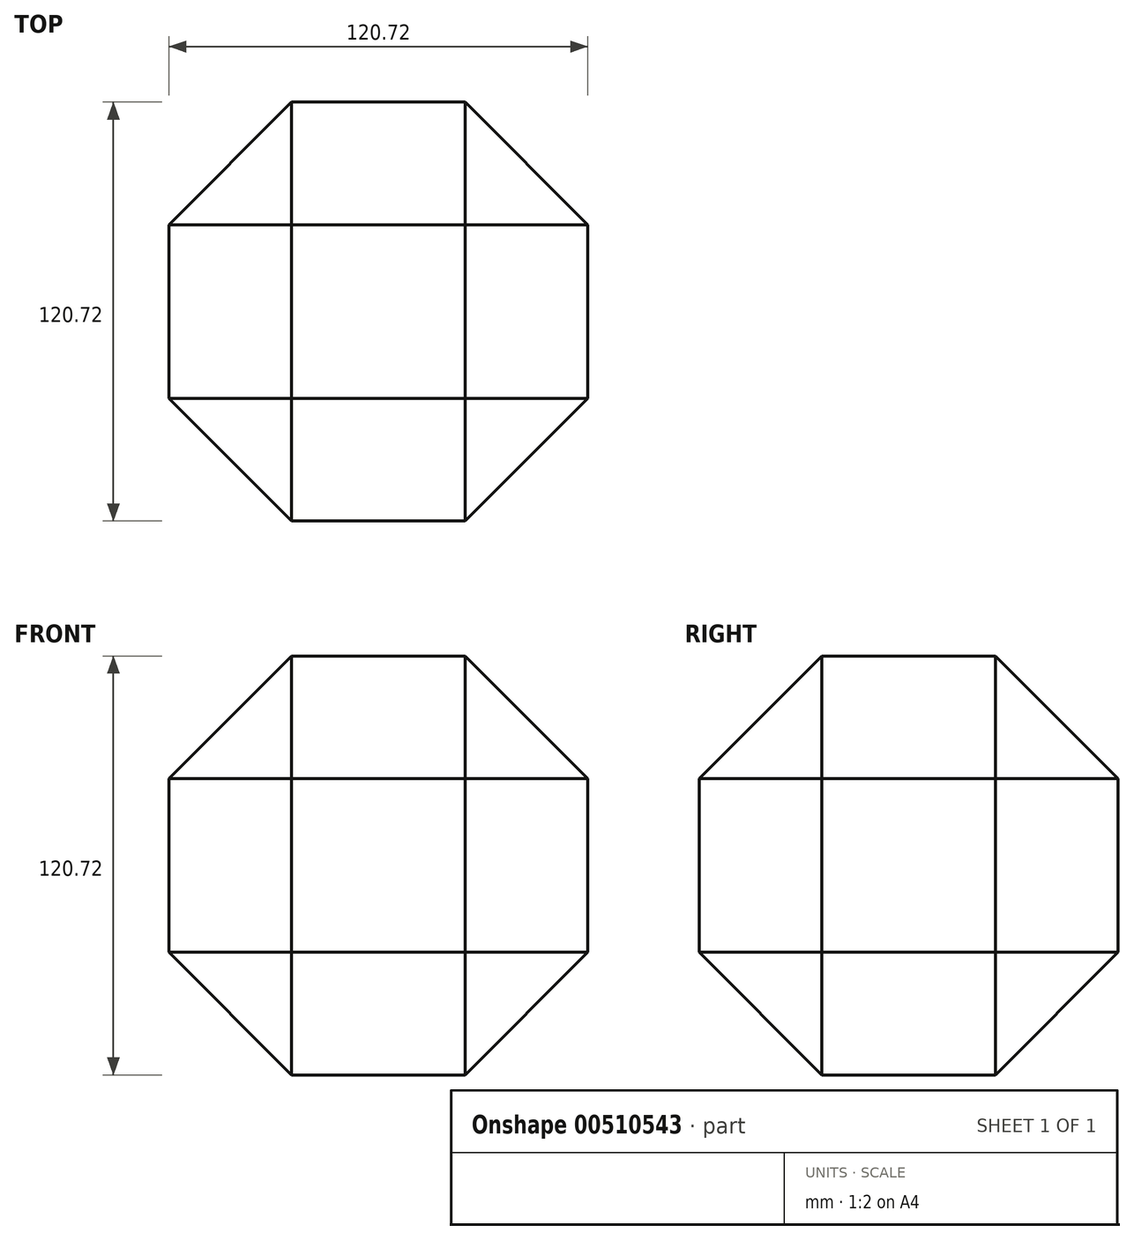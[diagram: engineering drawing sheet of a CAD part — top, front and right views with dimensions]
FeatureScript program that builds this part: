
annotation { "Feature Type Name" : "Feature", "Feature Type Description" : "" }
export const myFeature = defineFeature(function(context is Context, id is Id, definition is map)
    precondition{}
    {
        {
            assignVariable(context, id + "F0", {"name" : "Size", "anyValue" : 50});
        }
        {
            var Q0;
            Q0=qCreatedBy(makeId("Front.planeOp"),FACE);
            var sketch = newSketch(context, id + "F1", { "sketchPlane" : qUnion([Q0])});
            skLineSegment(sketch, "E0.bottom", {"start": v(25, 25) * mm, "end": v(-25, 25) * mm, "construction": true});
            skLineSegment(sketch, "E0.top", {"start": v(25, -25) * mm, "end": v(-25, -25) * mm, "construction": true});
            skLineSegment(sketch, "E0.left", {"start": v(25, 25) * mm, "end": v(25, -25) * mm, "construction": true});
            skLineSegment(sketch, "E0.right", {"start": v(-25, 25) * mm, "end": v(-25, -25) * mm, "construction": true});
            skPoint(sketch, "E0.middle", {"position": v(0, 0) * mm});
            skLineSegment(sketch, "E1", {"start": v(-25, 60.36) * mm, "end": v(25, 60.36) * mm});
            skLineSegment(sketch, "E2", {"start": v(25, 60.36) * mm, "end": v(60.36, 25) * mm});
            skLineSegment(sketch, "E3", {"start": v(60.36, 25) * mm, "end": v(60.36, -25) * mm});
            skLineSegment(sketch, "E4", {"start": v(60.36, -25) * mm, "end": v(25, -60.36) * mm});
            skLineSegment(sketch, "E5", {"start": v(25, -60.36) * mm, "end": v(-25, -60.36) * mm});
            skLineSegment(sketch, "E6", {"start": v(-25, -60.36) * mm, "end": v(-60.36, -25) * mm});
            skLineSegment(sketch, "E7", {"start": v(-60.36, -25) * mm, "end": v(-60.36, 25) * mm});
            skLineSegment(sketch, "E8", {"start": v(-60.36, 25) * mm, "end": v(-25, 60.36) * mm});
            skLineSegment(sketch, "E9", {"start": v(-60.36, 0) * mm, "end": v(-25, 0) * mm, "construction": true});
            skLineSegment(sketch, "E10", {"start": v(0, 25) * mm, "end": v(0, 60.36) * mm, "construction": true});
            skSolve(sketch);
        }
        {
            var Q0;
            Q0=makeQuery(id+"F1.imprint","IMPRINT",FACE,{"disambiguationData":[TD([[makeQuery(id+"F1.imprint","IMPRINT",EDGE,{"derivedFrom":sQuery(id+"F1.wireOp",EDGE,"E1")}),-1.0]])]});
            extrude(context, id + "F2", {"entities" : qUnion([Q0]), "depth" : (getVariable(context, 'Size') / 2) * mm, "hasSecondDirection" : true, "secondDirectionOppositeDirection" : true, "secondDirectionDepth" : (getVariable(context, 'Size') / 2) * mm});
        }
        {
            var Q0;
            Q0=qCreatedBy(makeId("Top.planeOp"),FACE);
            var sketch = newSketch(context, id + "F3", { "sketchPlane" : qUnion([Q0])});
            skLineSegment(sketch, "E11.bottom", {"start": v(25, 25) * mm, "end": v(-25, 25) * mm, "construction": true});
            skLineSegment(sketch, "E11.top", {"start": v(25, -25) * mm, "end": v(-25, -25) * mm, "construction": true});
            skLineSegment(sketch, "E11.left", {"start": v(25, 25) * mm, "end": v(25, -25) * mm, "construction": true});
            skLineSegment(sketch, "E11.right", {"start": v(-25, 25) * mm, "end": v(-25, -25) * mm, "construction": true});
            skPoint(sketch, "E11.middle", {"position": v(0, 0) * mm});
            skLineSegment(sketch, "E12", {"start": v(60.36, -25) * mm, "end": v(60.36, 25) * mm});
            skLineSegment(sketch, "E13", {"start": v(60.36, 25) * mm, "end": v(25, 60.36) * mm});
            skLineSegment(sketch, "E14", {"start": v(25, 60.36) * mm, "end": v(-25, 60.36) * mm});
            skLineSegment(sketch, "E15", {"start": v(-25, 60.36) * mm, "end": v(-60.36, 25) * mm});
            skLineSegment(sketch, "E16", {"start": v(-60.36, 25) * mm, "end": v(-60.36, -25) * mm});
            skLineSegment(sketch, "E17", {"start": v(-60.36, -25) * mm, "end": v(-25, -60.36) * mm});
            skLineSegment(sketch, "E18", {"start": v(-25, -60.36) * mm, "end": v(25, -60.36) * mm});
            skLineSegment(sketch, "E19", {"start": v(25, -60.36) * mm, "end": v(60.36, -25) * mm});
            skLineSegment(sketch, "E20", {"start": v(25, 0) * mm, "end": v(60.36, 0) * mm, "construction": true});
            skLineSegment(sketch, "E21", {"start": v(0, -25) * mm, "end": v(0, -60.36) * mm, "construction": true});
            skSolve(sketch);
        }
        {
            var Q0;
            Q0=makeQuery(id+"F3.imprint","IMPRINT",FACE,{"disambiguationData":[TD([[makeQuery(id+"F3.imprint","IMPRINT",EDGE,{"derivedFrom":sQuery(id+"F3.wireOp",EDGE,"E12")}),1.0]])]});
            extrude(context, id + "F4", {"entities" : qUnion([Q0]), "operationType" : NewBodyOperationType.ADD, "depth" : (getVariable(context, 'Size') / 2) * mm, "hasSecondDirection" : true, "secondDirectionOppositeDirection" : true, "secondDirectionDepth" : (getVariable(context, 'Size') / 2) * mm});
        }
        {
            var Q0;
            Q0=qCreatedBy(makeId("Right.planeOp"),FACE);
            var sketch = newSketch(context, id + "F5", { "sketchPlane" : qUnion([Q0])});
            skLineSegment(sketch, "E22.bottom", {"start": v(25, 25) * mm, "end": v(-25, 25) * mm, "construction": true});
            skLineSegment(sketch, "E22.top", {"start": v(25, -25) * mm, "end": v(-25, -25) * mm, "construction": true});
            skLineSegment(sketch, "E22.left", {"start": v(25, 25) * mm, "end": v(25, -25) * mm, "construction": true});
            skLineSegment(sketch, "E22.right", {"start": v(-25, 25) * mm, "end": v(-25, -25) * mm, "construction": true});
            skPoint(sketch, "E22.middle", {"position": v(0, 0) * mm});
            skLineSegment(sketch, "E23", {"start": v(25, 60.36) * mm, "end": v(-25, 60.36) * mm});
            skLineSegment(sketch, "E24", {"start": v(-25, 60.36) * mm, "end": v(-60.36, 25) * mm});
            skLineSegment(sketch, "E25", {"start": v(-60.36, 25) * mm, "end": v(-60.36, -25) * mm});
            skLineSegment(sketch, "E26", {"start": v(-60.36, -25) * mm, "end": v(-25, -60.36) * mm});
            skLineSegment(sketch, "E27", {"start": v(-25, -60.36) * mm, "end": v(25, -60.36) * mm});
            skLineSegment(sketch, "E28", {"start": v(25, -60.36) * mm, "end": v(60.36, -25) * mm});
            skLineSegment(sketch, "E29", {"start": v(60.36, -25) * mm, "end": v(60.36, 25) * mm});
            skLineSegment(sketch, "E30", {"start": v(60.36, 25) * mm, "end": v(25, 60.36) * mm});
            skLineSegment(sketch, "E31", {"start": v(0, 25) * mm, "end": v(0, 60.36) * mm, "construction": true});
            skLineSegment(sketch, "E32", {"start": v(25, 0) * mm, "end": v(60.36, 0) * mm, "construction": true});
            skSolve(sketch);
        }
        {
            var Q0;
            Q0=makeQuery(id+"F5.imprint","IMPRINT",FACE,{"disambiguationData":[TD([[makeQuery(id+"F5.imprint","IMPRINT",EDGE,{"derivedFrom":sQuery(id+"F5.wireOp",EDGE,"E23")}),1.0]])]});
            extrude(context, id + "F6", {"entities" : qUnion([Q0]), "operationType" : NewBodyOperationType.ADD, "depth" : (getVariable(context, 'Size') / 2) * mm, "hasSecondDirection" : true, "secondDirectionOppositeDirection" : true, "secondDirectionDepth" : (getVariable(context, 'Size') / 2) * mm});
        }
    });
